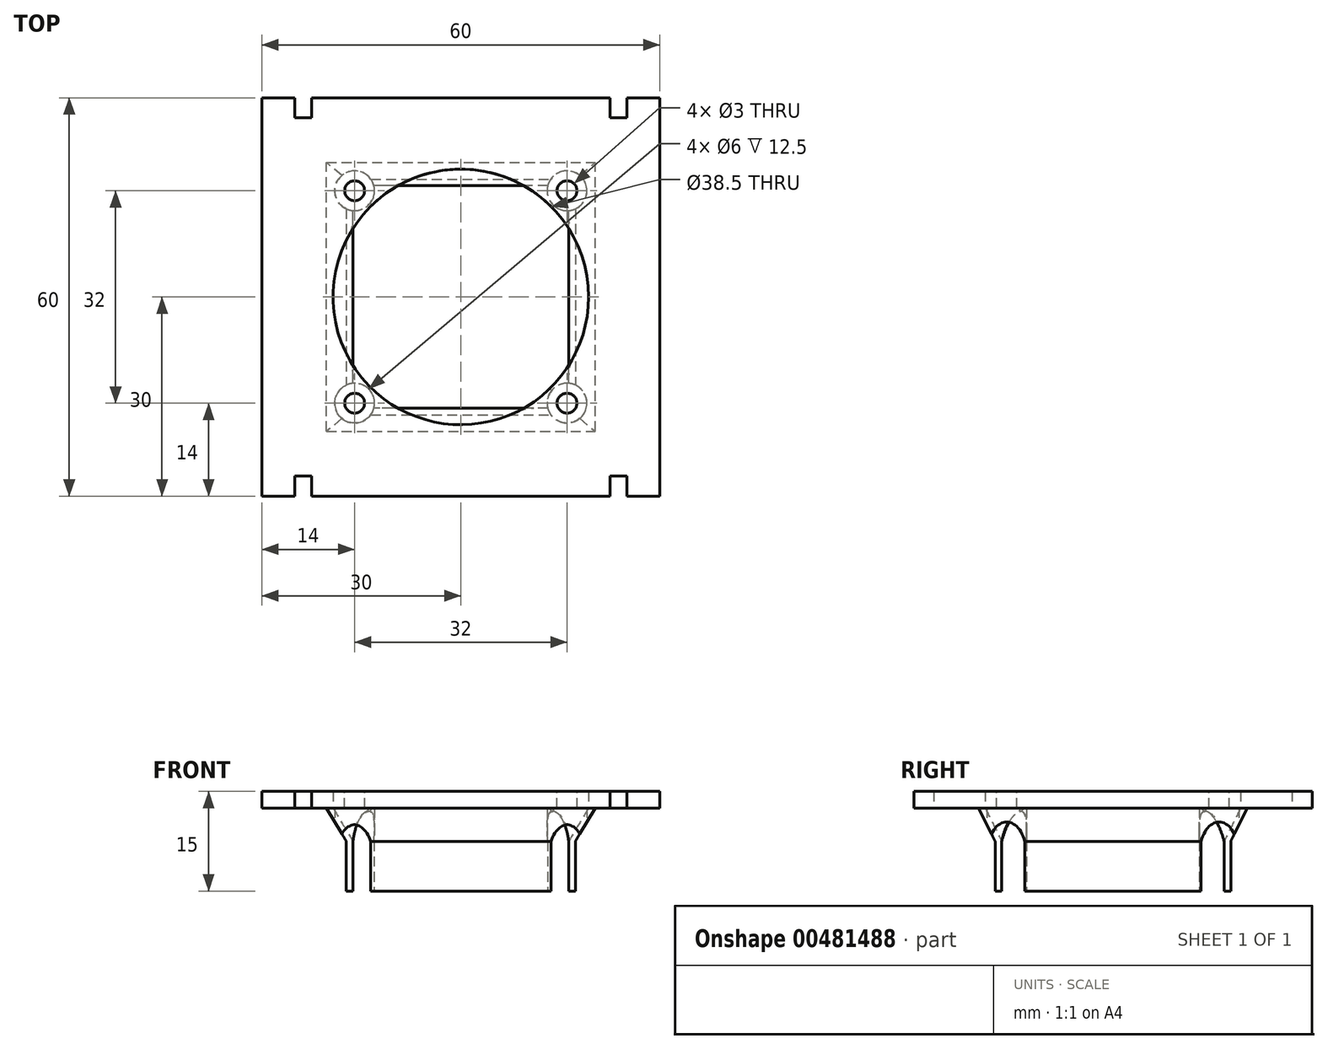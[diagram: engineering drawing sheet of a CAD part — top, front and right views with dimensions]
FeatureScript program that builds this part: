
annotation { "Feature Type Name" : "Feature", "Feature Type Description" : "" }
export const myFeature = defineFeature(function(context is Context, id is Id, definition is map)
    precondition{}
    {
        {
            var Q0;
            Q0=qCreatedBy(makeId("Top.planeOp"),FACE);
            var sketch = newSketch(context, id + "F0", { "sketchPlane" : qUnion([Q0])});
            skLineSegment(sketch, "E0.bottom", {"start": v(-16, 16) * mm, "end": v(16, 16) * mm, "construction": true});
            skLineSegment(sketch, "E0.top", {"start": v(-16, -16) * mm, "end": v(16, -16) * mm, "construction": true});
            skLineSegment(sketch, "E0.left", {"start": v(-16, 16) * mm, "end": v(-16, -16) * mm, "construction": true});
            skLineSegment(sketch, "E0.right", {"start": v(16, 16) * mm, "end": v(16, -16) * mm, "construction": true});
            skPoint(sketch, "E0.middle", {"position": v(0, 0) * mm});
            skLineSegment(sketch, "E1.bottom", {"start": v(-20, 20) * mm, "end": v(20, 20) * mm, "construction": true});
            skLineSegment(sketch, "E1.top", {"start": v(-20, -20) * mm, "end": v(20, -20) * mm, "construction": true});
            skLineSegment(sketch, "E1.left", {"start": v(-20, 20) * mm, "end": v(-20, -20) * mm, "construction": true});
            skLineSegment(sketch, "E1.right", {"start": v(20, 20) * mm, "end": v(20, -20) * mm, "construction": true});
            skCircle(sketch, "E2", {"center": v(0, 0) * mm, "radius": 19.25 * mm});
            skLineSegment(sketch, "E3.bottom", {"start": v(-30, 30) * mm, "end": v(-25, 30) * mm});
            skLineSegment(sketch, "E3.top", {"start": v(-30, -30) * mm, "end": v(-25, -30) * mm});
            skLineSegment(sketch, "E3.left", {"start": v(-30, 30) * mm, "end": v(-30, -30) * mm});
            skLineSegment(sketch, "E3.right", {"start": v(30, 30) * mm, "end": v(30, -30) * mm});
            skLineSegment(sketch, "E4.top", {"start": v(-25, 27) * mm, "end": v(-22.5, 27) * mm});
            skLineSegment(sketch, "E4.left", {"start": v(-25, 30) * mm, "end": v(-25, 27) * mm});
            skLineSegment(sketch, "E4.right", {"start": v(-22.5, 30) * mm, "end": v(-22.5, 27) * mm});
            skLineSegment(sketch, "E5.trimOffspring", {"start": v(-22.5, 30) * mm, "end": v(22.5, 30) * mm});
            skLineSegment(sketch, "E6.MirrorCS", {"start": v(-25, -30) * mm, "end": v(-25, -27) * mm});
            skLineSegment(sketch, "E7.MirrorCS", {"start": v(-25, -27) * mm, "end": v(-22.5, -27) * mm});
            skLineSegment(sketch, "E8.MirrorCS", {"start": v(-22.5, -30) * mm, "end": v(-22.5, -27) * mm});
            skLineSegment(sketch, "E9.trimOffspring", {"start": v(-22.5, -30) * mm, "end": v(22.5, -30) * mm});
            skLineSegment(sketch, "E10.MirrorCS", {"start": v(25, 30) * mm, "end": v(25, 27) * mm});
            skLineSegment(sketch, "E11.MirrorCS", {"start": v(25, 27) * mm, "end": v(22.5, 27) * mm});
            skLineSegment(sketch, "E12.MirrorCS", {"start": v(22.5, 30) * mm, "end": v(22.5, 27) * mm});
            skLineSegment(sketch, "E13.MirrorCS", {"start": v(25, -30) * mm, "end": v(25, -27) * mm});
            skLineSegment(sketch, "E14.MirrorCS", {"start": v(25, -27) * mm, "end": v(22.5, -27) * mm});
            skLineSegment(sketch, "E15.MirrorCS", {"start": v(22.5, -30) * mm, "end": v(22.5, -27) * mm});
            skLineSegment(sketch, "E16.trimOffspring", {"start": v(25, 30) * mm, "end": v(30, 30) * mm});
            skLineSegment(sketch, "E17.trimOffspring", {"start": v(25, -30) * mm, "end": v(30, -30) * mm});
            skSolve(sketch);
        }
        {
            var Q0;
            Q0 = qSketchRegion(id + "F0", true);
            extrude(context, id + "F1", {"entities" : qUnion([Q0]), "depth" : 2.5 * mm});
        }
        {
            var Q0;
            Q0=qCreatedBy(makeId("Top.planeOp"),FACE);
            cPlane(context, id + "F2", {"entities" : qUnion([Q0]), "cplaneType" : CPlaneType.OFFSET, "offset" : 5 * mm, "oppositeDirection" : true, "width" : 150 * mm, "height" : 150 * mm});
        }
        {
            var Q0;
            Q0=qCreatedBy(id+"F2.planeOp",FACE);
            var sketch = newSketch(context, id + "F3", { "sketchPlane" : qUnion([Q0])});
            skLineSegment(sketch, "E18.bottom", {"start": v(-17.25, 17.75) * mm, "end": v(17.25, 17.75) * mm});
            skLineSegment(sketch, "E18.top", {"start": v(-17.25, -17.75) * mm, "end": v(17.25, -17.75) * mm});
            skLineSegment(sketch, "E18.left", {"start": v(-17.25, 17.75) * mm, "end": v(-17.25, -17.75) * mm});
            skLineSegment(sketch, "E18.right", {"start": v(17.25, 17.75) * mm, "end": v(17.25, -17.75) * mm});
            skPoint(sketch, "E18.middle", {"position": v(0, 0) * mm});
            skSolve(sketch);
        }
        {
            var Q0;
            Q0=makeQuery(id+"F1.opExtrude","CAP_FACE",FACE,{"disambiguationData":[OSD([sQuery(id+"F0.wireOp",EDGE,"jvZsX8ok-99zj-d49R-lAZn-6nenmzq0dqQg"),sQuery(id+"F0.wireOp",EDGE,"VLr22JCP-fIiN-MNfw-bjUi-2veGQDJ6hksr"),sQuery(id+"F0.wireOp",EDGE,"GE5Nl5Fd-LKWN-4TJx-kHFe-WfOJgcmSfcMd"),sQuery(id+"F0.wireOp",EDGE,"d0YC339O-eHt6-lMAN-glLq-L8IC3gUBp3es"),sQuery(id+"F0.wireOp",EDGE,"E2"),sQuery(id+"F0.wireOp",EDGE,"E3.bottom"),sQuery(id+"F0.wireOp",EDGE,"E3.top"),sQuery(id+"F0.wireOp",EDGE,"E3.left"),sQuery(id+"F0.wireOp",EDGE,"E3.right"),sQuery(id+"F0.wireOp",EDGE,"E4.top"),sQuery(id+"F0.wireOp",EDGE,"E4.left"),sQuery(id+"F0.wireOp",EDGE,"E4.right"),sQuery(id+"F0.wireOp",EDGE,"E5.trimOffspring"),sQuery(id+"F0.wireOp",EDGE,"E6.MirrorCS"),sQuery(id+"F0.wireOp",EDGE,"E7.MirrorCS"),sQuery(id+"F0.wireOp",EDGE,"E8.MirrorCS"),sQuery(id+"F0.wireOp",EDGE,"E9.trimOffspring"),sQuery(id+"F0.wireOp",EDGE,"E10.MirrorCS"),sQuery(id+"F0.wireOp",EDGE,"E11.MirrorCS"),sQuery(id+"F0.wireOp",EDGE,"E12.MirrorCS"),sQuery(id+"F0.wireOp",EDGE,"E13.MirrorCS"),sQuery(id+"F0.wireOp",EDGE,"E14.MirrorCS"),sQuery(id+"F0.wireOp",EDGE,"E15.MirrorCS"),sQuery(id+"F0.wireOp",EDGE,"E16.trimOffspring"),sQuery(id+"F0.wireOp",EDGE,"E17.trimOffspring")])],"isStart":true});
            var sketch = newSketch(context, id + "F4", { "sketchPlane" : qUnion([Q0])});
            skLineSegment(sketch, "E19.bottom", {"start": v(-20.25, 20.25) * mm, "end": v(20.25, 20.25) * mm});
            skLineSegment(sketch, "E19.top", {"start": v(-20.25, -20.25) * mm, "end": v(20.25, -20.25) * mm});
            skLineSegment(sketch, "E19.left", {"start": v(-20.25, 20.25) * mm, "end": v(-20.25, -20.25) * mm});
            skLineSegment(sketch, "E19.right", {"start": v(20.25, 20.25) * mm, "end": v(20.25, -20.25) * mm});
            skPoint(sketch, "E19.middle", {"position": v(0, 0) * mm});
            skCircle(sketch, "E20.0", {"center": v(0, 0) * mm, "radius": 19.25 * mm, "construction": true});
            skSolve(sketch);
        }
        {
            var Q1;
            Q1 = qSketchRegion(id + "F3", true);
            var Q2;
            Q2 = qSketchRegion(id + "F4", true);
            loft(context, id + "F5", {"operationType" : NewBodyOperationType.ADD, "sheetProfilesArray" : [{ "sheetProfileEntities" : qUnion([Q1]) }, { "sheetProfileEntities" : qUnion([Q2]) }]});
        }
        {
            var Q0;
            Q0=makeQuery(id+"F3.imprint","IMPRINT",FACE,{"disambiguationData":[TD([[makeQuery(id+"F3.imprint","IMPRINT",EDGE,{"derivedFrom":sQuery(id+"F3.wireOp",EDGE,"E18.bottom")}),-1.0]])]});
            var sketch = newSketch(context, id + "F6", { "sketchPlane" : qUnion([Q0])});
            skLineSegment(sketch, "E21.bottom", {"start": v(16.25, -16.75) * mm, "end": v(-16.25, -16.75) * mm});
            skLineSegment(sketch, "E21.top", {"start": v(16.25, 16.75) * mm, "end": v(-16.25, 16.75) * mm});
            skLineSegment(sketch, "E21.left", {"start": v(16.25, -16.75) * mm, "end": v(16.25, 16.75) * mm});
            skLineSegment(sketch, "E21.right", {"start": v(-16.25, -16.75) * mm, "end": v(-16.25, 16.75) * mm});
            skPoint(sketch, "E21.middle", {"position": v(0, 0) * mm});
            skSolve(sketch);
        }
        {
            var Q1;
            Q1=makeQuery(id+"F6.imprint","IMPRINT",FACE,{"disambiguationData":[TD([[makeQuery(id+"F6.imprint","IMPRINT",EDGE,{"derivedFrom":sQuery(id+"F6.wireOp",EDGE,"E21.bottom")}),-1.0]])]});
            var Q2;
            Q2=makeQuery(id+"F4.imprint","IMPRINT",FACE,{"disambiguationData":[TD([[makeQuery(id+"F4.imprint","IMPRINT",EDGE,{"derivedFrom":makeQuery(id+"F1.opExtrude","CAP_EDGE",EDGE,{"disambiguationData":[OSD([sQuery(id+"F0.wireOp",EDGE,"E2")])],"isStart":true})}),-1.0]])]});
            loft(context, id + "F7", {"operationType" : NewBodyOperationType.REMOVE, "sheetProfilesArray" : [{ "sheetProfileEntities" : qUnion([Q1]) }, { "sheetProfileEntities" : qUnion([Q2]) }]});
        }
        {
            var Q0;
            Q0=makeQuery(id+"F5.opLoft","CAP_FACE",FACE,{"disambiguationData":[OSD([makeQuery(id+"F3.imprint","IMPRINT",FACE,{"disambiguationData":[TD([[makeQuery(id+"F3.imprint","IMPRINT",EDGE,{"derivedFrom":sQuery(id+"F3.wireOp",EDGE,"E18.bottom")}),-1.0]])]})])],"isStart":true});
            extrude(context, id + "F8", {"entities" : qUnion([Q0]), "operationType" : NewBodyOperationType.ADD, "depth" : 7.5 * mm});
        }
        {
            var Q0;
            Q0=makeQuery(id+"F1.opExtrude","CAP_FACE",FACE,{"disambiguationData":[OSD([sQuery(id+"F0.wireOp",EDGE,"E2"),sQuery(id+"F0.wireOp",EDGE,"E3.bottom"),sQuery(id+"F0.wireOp",EDGE,"E3.top"),sQuery(id+"F0.wireOp",EDGE,"E3.left"),sQuery(id+"F0.wireOp",EDGE,"E3.right"),sQuery(id+"F0.wireOp",EDGE,"E4.top"),sQuery(id+"F0.wireOp",EDGE,"E4.left"),sQuery(id+"F0.wireOp",EDGE,"E4.right"),sQuery(id+"F0.wireOp",EDGE,"E5.trimOffspring"),sQuery(id+"F0.wireOp",EDGE,"E6.MirrorCS"),sQuery(id+"F0.wireOp",EDGE,"E7.MirrorCS"),sQuery(id+"F0.wireOp",EDGE,"E8.MirrorCS"),sQuery(id+"F0.wireOp",EDGE,"E9.trimOffspring"),sQuery(id+"F0.wireOp",EDGE,"E10.MirrorCS"),sQuery(id+"F0.wireOp",EDGE,"E11.MirrorCS"),sQuery(id+"F0.wireOp",EDGE,"E12.MirrorCS"),sQuery(id+"F0.wireOp",EDGE,"E13.MirrorCS"),sQuery(id+"F0.wireOp",EDGE,"E14.MirrorCS"),sQuery(id+"F0.wireOp",EDGE,"E15.MirrorCS"),sQuery(id+"F0.wireOp",EDGE,"E16.trimOffspring"),sQuery(id+"F0.wireOp",EDGE,"E17.trimOffspring")])],"isStart":false});
            var sketch = newSketch(context, id + "F9", { "sketchPlane" : qUnion([Q0])});
            skLineSegment(sketch, "E22.bottom", {"start": v(-16, 16) * mm, "end": v(16, 16) * mm, "construction": true});
            skLineSegment(sketch, "E22.top", {"start": v(-16, -16) * mm, "end": v(16, -16) * mm, "construction": true});
            skLineSegment(sketch, "E22.left", {"start": v(-16, 16) * mm, "end": v(-16, -16) * mm, "construction": true});
            skLineSegment(sketch, "E22.right", {"start": v(16, 16) * mm, "end": v(16, -16) * mm, "construction": true});
            skPoint(sketch, "E22.middle", {"position": v(0, 0) * mm});
            skCircle(sketch, "E23", {"center": v(-16, 16) * mm, "radius": 1.5 * mm});
            skCircle(sketch, "E24.MirrorC", {"center": v(16, 16) * mm, "radius": 1.5 * mm});
            skCircle(sketch, "E25.MirrorC", {"center": v(-16, -16) * mm, "radius": 1.5 * mm});
            skCircle(sketch, "E26.MirrorC", {"center": v(16, -16) * mm, "radius": 1.5 * mm});
            skSolve(sketch);
        }
        {
            var Q0;
            Q0 = qSketchRegion(id + "F9", true);
            extrude(context, id + "F10", {"entities" : qUnion([Q0]), "operationType" : NewBodyOperationType.REMOVE, "endBound" : BoundingType.THROUGH_ALL, "oppositeDirection" : true, "depth" : 25 * mm});
        }
        {
            var Q0;
            {var subQ2=sQuery(id+"F3.wireOp",EDGE,"E18.bottom");Q0=makeQuery(id+"F10.boolean.opBoolean","SPLIT",FACE,{"disambiguationData":[TD([makeQuery(id+"F8.opExtrude","SWEPT_FACE",FACE,{"disambiguationData":[OSD([sQuery(id+"F6.wireOp",EDGE,"E21.bottom"),sQuery(id+"F6.wireOp",EDGE,"E21.top"),sQuery(id+"F6.wireOp",EDGE,"E21.left")])]})])],"derivedFrom":makeQuery(id+"F8.opExtrude","CAP_FACE",FACE,{"disambiguationData":[OSD([makeQuery(id+"F3.imprint","IMPRINT",FACE,{"disambiguationData":[TD([[makeQuery(id+"F3.imprint","IMPRINT",EDGE,{"derivedFrom":subQ2}),-1.0]])]})])],"isStart":false})});}
            var sketch = newSketch(context, id + "F11", { "sketchPlane" : qUnion([Q0])});
            skCircle(sketch, "E27.0", {"center": v(-16, -16) * mm, "radius": 1.5 * mm, "construction": true});
            skCircle(sketch, "E27.1", {"center": v(-16, 16) * mm, "radius": 1.5 * mm, "construction": true});
            skCircle(sketch, "E27.2", {"center": v(16, 16) * mm, "radius": 1.5 * mm, "construction": true});
            skCircle(sketch, "E27.3", {"center": v(16, -16) * mm, "radius": 1.5 * mm, "construction": true});
            skCircle(sketch, "E28", {"center": v(-16, 16) * mm, "radius": 3 * mm});
            skCircle(sketch, "E29.MirrorC", {"center": v(16, 16) * mm, "radius": 3 * mm});
            skCircle(sketch, "E30.MirrorC", {"center": v(-16, -16) * mm, "radius": 3 * mm});
            skCircle(sketch, "E31.MirrorC", {"center": v(16, -16) * mm, "radius": 3 * mm});
            skSolve(sketch);
        }
        {
            var Q0;
            Q0 = qSketchRegion(id + "F11", true);
            var Q1;
            Q1=makeQuery(id+"F1.opExtrude","CAP_FACE",FACE,{"disambiguationData":[OSD([sQuery(id+"F0.wireOp",EDGE,"E2"),sQuery(id+"F0.wireOp",EDGE,"E3.bottom"),sQuery(id+"F0.wireOp",EDGE,"E3.top"),sQuery(id+"F0.wireOp",EDGE,"E3.left"),sQuery(id+"F0.wireOp",EDGE,"E3.right"),sQuery(id+"F0.wireOp",EDGE,"E4.top"),sQuery(id+"F0.wireOp",EDGE,"E4.left"),sQuery(id+"F0.wireOp",EDGE,"E4.right"),sQuery(id+"F0.wireOp",EDGE,"E5.trimOffspring"),sQuery(id+"F0.wireOp",EDGE,"E6.MirrorCS"),sQuery(id+"F0.wireOp",EDGE,"E7.MirrorCS"),sQuery(id+"F0.wireOp",EDGE,"E8.MirrorCS"),sQuery(id+"F0.wireOp",EDGE,"E9.trimOffspring"),sQuery(id+"F0.wireOp",EDGE,"E10.MirrorCS"),sQuery(id+"F0.wireOp",EDGE,"E11.MirrorCS"),sQuery(id+"F0.wireOp",EDGE,"E12.MirrorCS"),sQuery(id+"F0.wireOp",EDGE,"E13.MirrorCS"),sQuery(id+"F0.wireOp",EDGE,"E14.MirrorCS"),sQuery(id+"F0.wireOp",EDGE,"E15.MirrorCS"),sQuery(id+"F0.wireOp",EDGE,"E16.trimOffspring"),sQuery(id+"F0.wireOp",EDGE,"E17.trimOffspring")])],"isStart":true});
            extrude(context, id + "F12", {"entities" : qUnion([Q0]), "operationType" : NewBodyOperationType.REMOVE, "endBound" : BoundingType.UP_TO_SURFACE, "oppositeDirection" : true, "endBoundEntityFace" : qUnion([Q1]), "depth" : 11.1 * mm});
        }
    });
